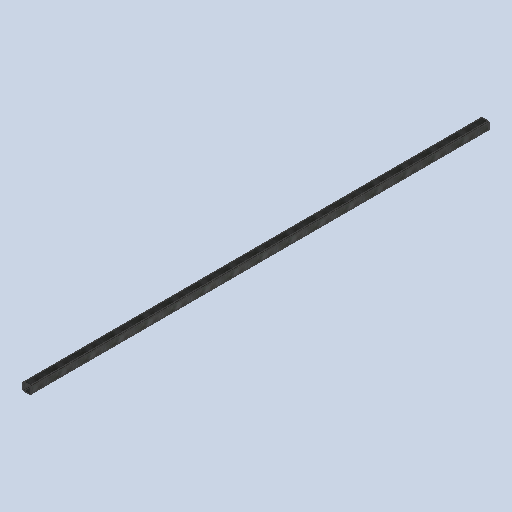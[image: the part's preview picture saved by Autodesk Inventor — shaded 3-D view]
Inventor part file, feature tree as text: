
AUTODESK INVENTOR PART (.ipt)
format: ipt  version: 2025 (Build 290162010, 162A)  size: 114,176 bytes
history: native  units: mm
features: extrude x1, sketch x1
ambient origin geometry x8: Origin, YZ Plane, XZ Plane, XY Plane, X Axis, Y Axis, Z Axis, Center Point
bodies: Solid1 (feature_tree)
feature tree (2):
  extrude  "Extrusion1"  Depth=6.0mm
  sketch  "Sketch1"  dims[d0=6.0mm d1=50.0mm d2=50.0mm d3=2.0mm d6=6.0mm d7=100.0mm d8=100.0mm d9=3.0mm d10=2797.0mm d11=0.0mm]
